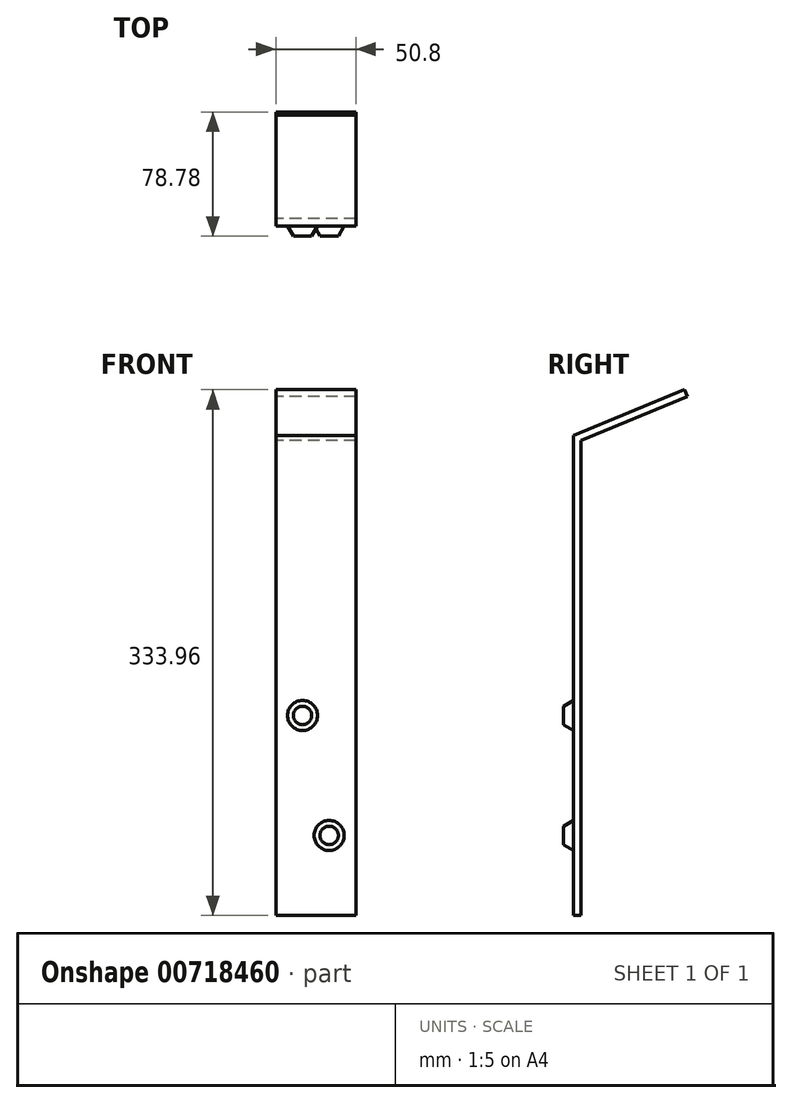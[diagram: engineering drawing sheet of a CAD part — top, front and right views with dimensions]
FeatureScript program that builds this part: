
annotation { "Feature Type Name" : "Feature", "Feature Type Description" : "" }
export const myFeature = defineFeature(function(context is Context, id is Id, definition is map)
    precondition{}
    {
        {
            var Q0;
            Q0=qCreatedBy(makeId("Right.planeOp"),FACE);
            var sketch = newSketch(context, id + "F0", { "sketchPlane" : qUnion([Q0])});
            skLineSegment(sketch, "E0", {"start": v(0, 0) * mm, "end": v(0, 304.8) * mm});
            skLineSegment(sketch, "E1", {"start": v(0, 304.8) * mm, "end": v(70.4, 333.96) * mm});
            skLineSegment(sketch, "E2.0", {"start": v(4.76, 301.62) * mm, "end": v(72.43, 329.65) * mm});
            skLineSegment(sketch, "E2.1", {"start": v(4.76, 0) * mm, "end": v(4.76, 301.62) * mm});
            skLineSegment(sketch, "E3", {"start": v(70.4, 333.96) * mm, "end": v(72.43, 329.65) * mm});
            skLineSegment(sketch, "E4", {"start": v(0, 0) * mm, "end": v(4.76, 0) * mm});
            skSolve(sketch);
        }
        {
            var Q0;
            Q0 = qSketchRegion(id + "F0", true);
            extrude(context, id + "F1", {"entities" : qUnion([Q0]), "depth" : 50.8 * mm, "offsetDistance" : 25.4 * mm});
        }
        {
            var Q0;
            Q0=makeQuery(id+"F1.opExtrude","SWEPT_FACE",FACE,{"disambiguationData":[OSD([sQuery(id+"F0.wireOp",EDGE,"E0")])]});
            var sketch = newSketch(context, id + "F2", { "sketchPlane" : qUnion([Q0])});
            skCircle(sketch, "E5", {"center": v(16.93, 127) * mm, "radius": 9.53 * mm});
            skCircle(sketch, "E6", {"center": v(33.87, 50.8) * mm, "radius": 9.53 * mm});
            skSolve(sketch);
        }
        {
            var Q0;
            Q0=makeQuery(id+"F2.imprint","IMPRINT",FACE,{"disambiguationData":[TD([[makeQuery(id+"F2.imprint","IMPRINT",EDGE,{"derivedFrom":sQuery(id+"F2.wireOp",EDGE,"qvPwQMCX-jN1t-Y6J5-VbqX-tno2NA3bNXuE")}),1.0]])]});
            var Q1;
            Q1=makeQuery(id+"F2.imprint","IMPRINT",FACE,{"disambiguationData":[TD([[makeQuery(id+"F2.imprint","IMPRINT",EDGE,{"derivedFrom":sQuery(id+"F2.wireOp",EDGE,"wLCkn5JT-XvnV-zWry-BgDY-EvwVFihYtlV1")}),1.0]])]});
            var Q2;
            Q2=makeQuery(id+"F2.imprint","IMPRINT",FACE,{"disambiguationData":[TD([[makeQuery(id+"F2.imprint","IMPRINT",EDGE,{"derivedFrom":sQuery(id+"F2.wireOp",EDGE,"E5")}),1.0]])]});
            var Q3;
            Q3=makeQuery(id+"F2.imprint","IMPRINT",FACE,{"disambiguationData":[TD([[makeQuery(id+"F2.imprint","IMPRINT",EDGE,{"derivedFrom":sQuery(id+"F2.wireOp",EDGE,"E6")}),1.0]])]});
            extrude(context, id + "F3", {"entities" : qUnion([Q0, Q1, Q2, Q3]), "operationType" : NewBodyOperationType.ADD, "depth" : 6.35 * mm, "offsetDistance" : 25.4 * mm, "hasDraft" : true, "draftAngle" : 30 * degree, "draftPullDirection" : true});
        }
    });
